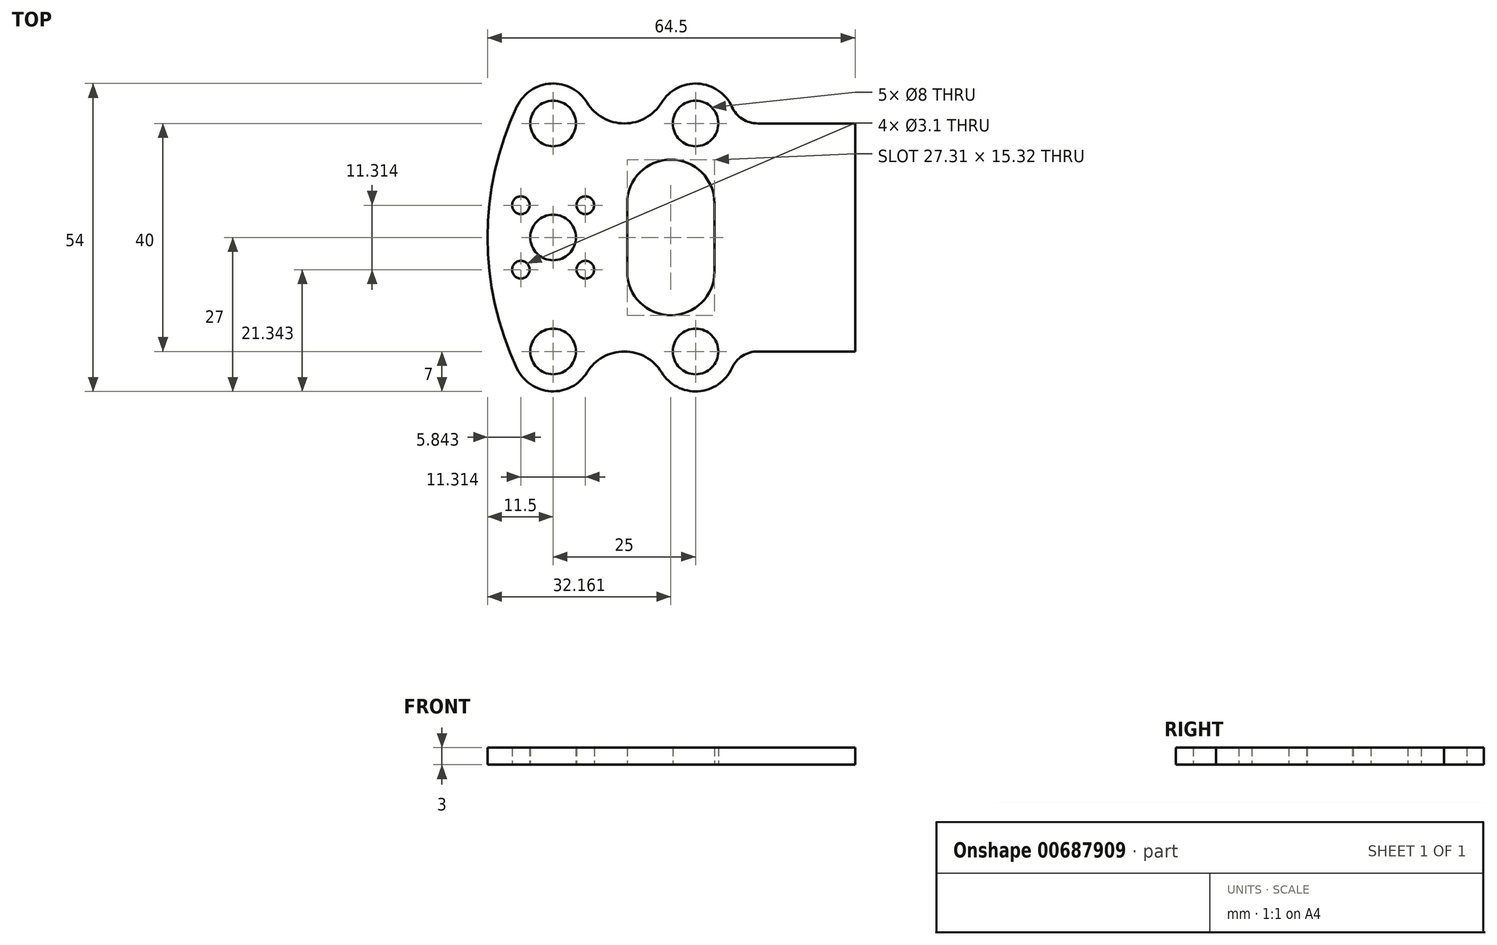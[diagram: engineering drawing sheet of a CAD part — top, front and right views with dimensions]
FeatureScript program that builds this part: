
annotation { "Feature Type Name" : "Feature", "Feature Type Description" : "" }
export const myFeature = defineFeature(function(context is Context, id is Id, definition is map)
    precondition{}
    {
        {
            var Q0;
            Q0=qCreatedBy(makeId("Top.planeOp"),FACE);
            var sketch = newSketch(context, id + "F0", { "sketchPlane" : qUnion([Q0])});
            skLineSegment(sketch, "E0.bottom", {"start": v(25, 20) * mm, "end": v(0, 20) * mm, "construction": true});
            skLineSegment(sketch, "E0.top", {"start": v(25, -20) * mm, "end": v(0, -20) * mm, "construction": true});
            skLineSegment(sketch, "E0.left", {"start": v(25, 20) * mm, "end": v(25, -20) * mm, "construction": true});
            skLineSegment(sketch, "E0.right", {"start": v(0, 20) * mm, "end": v(0, -20) * mm, "construction": true});
            skCircle(sketch, "E1", {"center": v(25, 20) * mm, "radius": 4 * mm});
            skCircle(sketch, "E2", {"center": v(25, -20) * mm, "radius": 4 * mm});
            skCircle(sketch, "E3", {"center": v(0, -20) * mm, "radius": 4 * mm});
            skCircle(sketch, "E4", {"center": v(0, 20) * mm, "radius": 4 * mm});
            skCircle(sketch, "E5", {"center": v(5.66, -5.66) * mm, "radius": 1.55 * mm});
            skCircle(sketch, "E6", {"center": v(-5.66, -5.66) * mm, "radius": 1.55 * mm});
            skCircle(sketch, "E7", {"center": v(-5.66, 5.66) * mm, "radius": 1.55 * mm});
            skCircle(sketch, "E8", {"center": v(5.66, 5.66) * mm, "radius": 1.55 * mm});
            skArc(sketch, "E9", {"start": v(5.97, 23.66) * mm, "mid": v(-0.37, 26.99) * mm, "end": v(-6.33, 23) * mm});
            skArc(sketch, "E10", {"start": v(-6.33, -23) * mm, "mid": v(-0.37, -26.99) * mm, "end": v(5.97, -23.66) * mm});
            skArc(sketch, "E11", {"start": v(19.03, -23.66) * mm, "mid": v(25.42, -26.99) * mm, "end": v(31.36, -22.92) * mm});
            skArc(sketch, "E12", {"start": v(5.97, 23.66) * mm, "mid": v(12.5, 20) * mm, "end": v(19.03, 23.66) * mm});
            skArc(sketch, "E13", {"start": v(19.03, -23.66) * mm, "mid": v(12.5, -20) * mm, "end": v(5.97, -23.66) * mm});
            skArc(sketch, "E14", {"start": v(28.32, 6) * mm, "mid": v(20.66, 13.66) * mm, "end": v(13, 6) * mm});
            skArc(sketch, "E15", {"start": v(13, -6) * mm, "mid": v(20.66, -13.66) * mm, "end": v(28.32, -6) * mm});
            skCircle(sketch, "E16", {"center": v(0, 0) * mm, "radius": 8 * mm, "construction": true});
            skLineSegment(sketch, "E17.bottom", {"start": v(5.66, -5.66) * mm, "end": v(-5.66, -5.66) * mm, "construction": true});
            skLineSegment(sketch, "E17.top", {"start": v(5.66, 5.66) * mm, "end": v(-5.66, 5.66) * mm, "construction": true});
            skLineSegment(sketch, "E17.left", {"start": v(5.66, -5.66) * mm, "end": v(5.66, 5.66) * mm, "construction": true});
            skLineSegment(sketch, "E17.right", {"start": v(-5.66, -5.66) * mm, "end": v(-5.66, 5.66) * mm, "construction": true});
            skCircle(sketch, "E18", {"center": v(0, 0) * mm, "radius": 4 * mm});
            skArc(sketch, "E19.trimOffspring", {"start": v(31.36, 22.92) * mm, "mid": v(25.42, 26.99) * mm, "end": v(19.03, 23.66) * mm});
            skArc(sketch, "E20", {"start": v(-6.33, 23) * mm, "mid": v(-11.5, 0) * mm, "end": v(-6.33, -23) * mm});
            skLineSegment(sketch, "E21", {"start": v(13, 6) * mm, "end": v(13, -6) * mm});
            skLineSegment(sketch, "E22", {"start": v(35.9, 20) * mm, "end": v(53, 20) * mm});
            skLineSegment(sketch, "E23", {"start": v(53, 20) * mm, "end": v(53, -20) * mm});
            skLineSegment(sketch, "E24", {"start": v(53, -20) * mm, "end": v(35.9, -20) * mm});
            skArc(sketch, "E25", {"start": v(31.36, 22.92) * mm, "mid": v(33.2, 20.8) * mm, "end": v(35.9, 20) * mm});
            skArc(sketch, "E26", {"start": v(35.9, -20) * mm, "mid": v(33.2, -20.8) * mm, "end": v(31.36, -22.92) * mm});
            skLineSegment(sketch, "E27", {"start": v(28.32, 6) * mm, "end": v(28.32, -6) * mm});
            skSolve(sketch);
        }
        {
            var Q0;
            Q0=makeQuery(id+"F0.imprint","IMPRINT",FACE,{"disambiguationData":[TD([[makeQuery(id+"F0.imprint","IMPRINT",EDGE,{"derivedFrom":sQuery(id+"F0.wireOp",EDGE,"E1")}),-1.0]])]});
            extrude(context, id + "F1", {"entities" : qUnion([Q0]), "depth" : 3 * mm, "offsetDistance" : 25 * mm});
        }
    });
